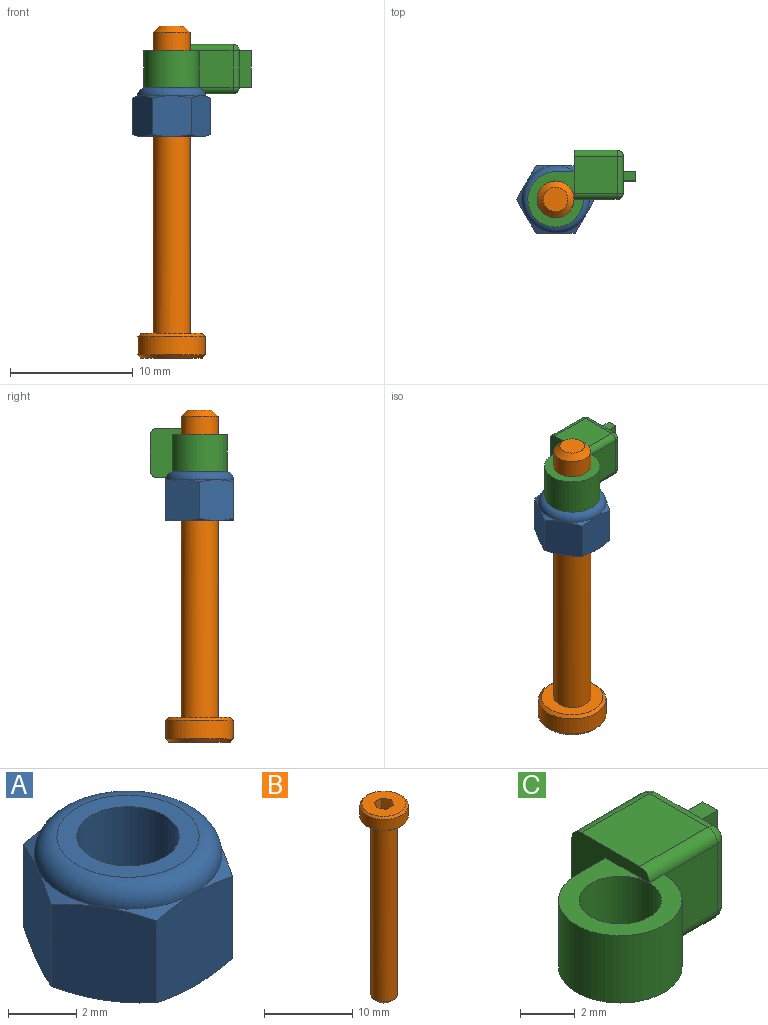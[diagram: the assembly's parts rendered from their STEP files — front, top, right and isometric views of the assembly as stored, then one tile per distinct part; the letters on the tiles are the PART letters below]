
ASSEMBLY  parts=3 mates=1
PART A: 22 faces, bbox 6.6x6.6x4.2 mm
  f0: plane 3.59x2.99mm, normal (-0.87,0.5,0), area 10.2mm2, adj f1,f5,f7,f9,f13,f14,f16,f21
  f1: plane 3.59x2.99mm, normal (-0.87,-0.5,0), area 10.2mm2, adj f0,f2,f7,f9,f10,f14,f20,f21
  f2: plane 3.6x3.42mm, normal (0,-1,0), area 10.2mm2, adj f1,f3,f7,f10,f11,f14,f19,f20
  f3: plane 3.59x2.99mm, normal (0.87,-0.5,0), area 10.2mm2, adj f2,f4,f7,f11,f12,f14,f18,f19
  f4: plane 3.59x2.99mm, normal (0.87,0.5,0), area 10.2mm2, adj f3,f5,f7,f12,f14,f15,f17,f18
  f5: plane 3.6x3.42mm, normal (0,1,0), area 10.2mm2, adj f0,f4,f7,f13,f14,f15,f16,f17
  f6: plane 4.17x4.17mm, normal (0,0,1), area 6.6mm2, adj f8,f14
  f7: plane 5.5x5.5mm, normal (0,0,-1), area 16.7mm2, adj f0,f1,f2,f3,f4,f5,f8,f16
  f8: cylinder r=1.5mm len=4mm, axis (0,0,1), area 37.7mm2, adj f6,f7
  f9: cone r=3.18mm half-angle=65deg, axis (0,0,-1), area 0.7mm2, adj f0,f1,f14
  f10: cone r=3.18mm half-angle=65deg, axis (0,0,-1), area 0.7mm2, adj f1,f2,f14
  f11: cone r=3.18mm half-angle=65deg, axis (0,0,-1), area 0.7mm2, adj f2,f3,f14
  f12: cone r=3.18mm half-angle=65deg, axis (0,0,-1), area 0.7mm2, adj f3,f4,f14
  f13: cone r=3.18mm half-angle=65deg, axis (0,0,-1), area 0.7mm2, adj f0,f5,f14
  f14: torus R=2.08mm, axis (0,0,-1), area 16.5mm2, adj f0,f1,f2,f3,f4,f5,f6,f9
  f15: cone r=3.18mm half-angle=65deg, axis (0,0,-1), area 0.7mm2, adj f4,f5,f14
  f16: cone r=2.75mm half-angle=65deg, axis (0,0,1), area 0.7mm2, adj f0,f5,f7
  f17: cone r=2.75mm half-angle=65deg, axis (0,0,1), area 0.7mm2, adj f4,f5,f7
  f18: cone r=2.75mm half-angle=65deg, axis (0,0,1), area 0.7mm2, adj f3,f4,f7
  f19: cone r=2.75mm half-angle=65deg, axis (0,0,1), area 0.7mm2, adj f2,f3,f7
  f20: cone r=2.75mm half-angle=65deg, axis (0,0,1), area 0.7mm2, adj f1,f2,f7
  f21: cone r=2.75mm half-angle=65deg, axis (0,0,1), area 0.7mm2, adj f0,f1,f7
PART B: 15 faces, bbox 5.5x5.5x27 mm
  f0: plane 5x5mm, normal (0,0,1), area 16.2mm2, adj f3,f4,f5,f6,f7,f8,f11
  f1: cylinder r=2.75mm len=5.5mm, axis (0,0,-1), area 25.9mm2, adj f10,f11
  f2: plane 5x5mm, normal (0,0,-1), area 12.6mm2, adj f10,f12
  f3: plane 1.5x1mm, normal (-0.87,-0.5,0), area 1.7mm2, adj f0,f4,f8,f9
  f4: plane 1.5x1.15mm, normal (0,-1,0), area 1.7mm2, adj f0,f3,f5,f9
  f5: plane 1.5x1mm, normal (0.87,-0.5,0), area 1.7mm2, adj f0,f4,f6,f9
  f6: plane 1.5x1mm, normal (0.87,0.5,0), area 1.7mm2, adj f0,f5,f7,f9
  f7: plane 1.5x1.15mm, normal (0,1,0), area 1.7mm2, adj f0,f6,f8,f9
  f8: plane 1.5x1mm, normal (-0.87,0.5,0), area 1.7mm2, adj f0,f3,f7,f9
  f9: plane 2.31x2mm, normal (0,0,1), area 3.5mm2, adj f3,f4,f5,f6,f7,f8
  f10: cone r=2.75mm half-angle=45deg, axis (0,0,1), area 5.8mm2, adj f1,f2
  f11: cone r=2.5mm half-angle=45deg, axis (0,0,-1), area 5.8mm2, adj f0,f1
  f12: cylinder r=1.5mm len=24.5mm, axis (0,0,1), area 230.9mm2, adj f2,f14
  f13: plane 2x2mm, normal (0,0,-1), area 3.1mm2, adj f14
  f14: cone r=1mm half-angle=45deg, axis (0,0,1), area 5.6mm2, adj f12,f13
PART C: 29 faces, bbox 8.8x6.3x4 mm
  f0: plane 3x1.25mm, normal (1,0,0), area 3.8mm2, adj f13,f18,f23,f24
  f1: cylinder r=2.25mm len=4.5mm, axis (0,0,-1), area 31.8mm2, adj f3,f4,f6,f16
  f2: cylinder r=1.5mm len=3mm, axis (0,0,-1), area 28.3mm2, adj f3,f4
  f3: plane 4.5x4.5mm, normal (0,0,1), area 8.2mm2, adj f1,f2,f5,f16,f22
  f4: plane 4.5x4.5mm, normal (0,0,-1), area 8.2mm2, adj f1,f2,f5,f16,f25
  f5: plane 4x4mm, normal (-1,0,0), area 9mm2, adj f3,f4,f8,f9,f10,f16,f17,f19
  f6: plane 3x2.75mm, normal (0,-1,0), area 8.2mm2, adj f1,f22,f25,f28
  f7: plane 3x1mm, normal (1,0,0), area 3mm2, adj f14,f23,f24,f28
  f8: plane 3.5x3mm, normal (0,1,0), area 10.5mm2, adj f5,f17,f18,f19
  f9: plane 3.5x3mm, normal (0,0,1), area 10.5mm2, adj f5,f17,f22,f23
  f10: plane 3.5x3mm, normal (0,0,-1), area 10.5mm2, adj f5,f19,f24,f25
  f11: plane 3x0.75mm, normal (1,0,0), area 2.2mm2, adj f12,f13,f14,f15
  f12: plane 1x0.75mm, normal (0,0,1), area 0.8mm2, adj f11,f13,f14,f23
  f13: plane 3x1mm, normal (0,1,0), area 3mm2, adj f0,f11,f12,f15
  f14: plane 3x1mm, normal (0,-1,0), area 3mm2, adj f7,f11,f12,f15
  f15: plane 1x0.75mm, normal (0,0,-1), area 0.8mm2, adj f11,f13,f14,f24
  f16: plane 3x1.5mm, normal (0,1,0), area 4.5mm2, adj f1,f3,f4,f5
  f17: cylinder r=0.5mm len=3.5mm, axis (1,0,0), area 2.7mm2, adj f5,f8,f9,f20
  f18: cylinder r=0.5mm len=3mm, axis (0,0,1), area 2.4mm2, adj f0,f8,f20,f21
  f19: cylinder r=0.5mm len=3.5mm, axis (-1,0,0), area 2.7mm2, adj f5,f8,f10,f21
  f20: sphere r=0.5mm, area 0.4mm2, adj f17,f18,f23
  f21: sphere r=0.5mm, area 0.4mm2, adj f18,f19,f24
  f22: cylinder r=0.5mm len=3.5mm, axis (-1,0,0), area 2.7mm2, adj f3,f5,f6,f9,f26
  f23: cylinder r=0.5mm len=3mm, axis (0,-1,0), area 2.4mm2, adj f0,f7,f9,f12,f20,f26
  f24: cylinder r=0.5mm len=3mm, axis (0,1,0), area 2.4mm2, adj f0,f7,f10,f15,f21,f27
  f25: cylinder r=0.5mm len=3.5mm, axis (1,0,0), area 2.7mm2, adj f4,f5,f6,f10,f27
  f26: sphere r=0.5mm, area 0.4mm2, adj f22,f23,f28
  f27: sphere r=0.5mm, area 0.4mm2, adj f24,f25,f28
  f28: cylinder r=0.5mm len=3mm, axis (0,0,-1), area 2.4mm2, adj f6,f7,f26,f27
PLACE A t=(-22.55,-24.82,1.81)mm
PLACE B rot(axis=(1,0,0),180deg) t=(27.45,-24.82,-14.19)mm
PLACE C t=(-22.55,-24.82,5.81)mm
MATE fastened B.f1 <-> A.f8  axis (0,0,1) through (-22.55,-24.82,-14.19)mm
